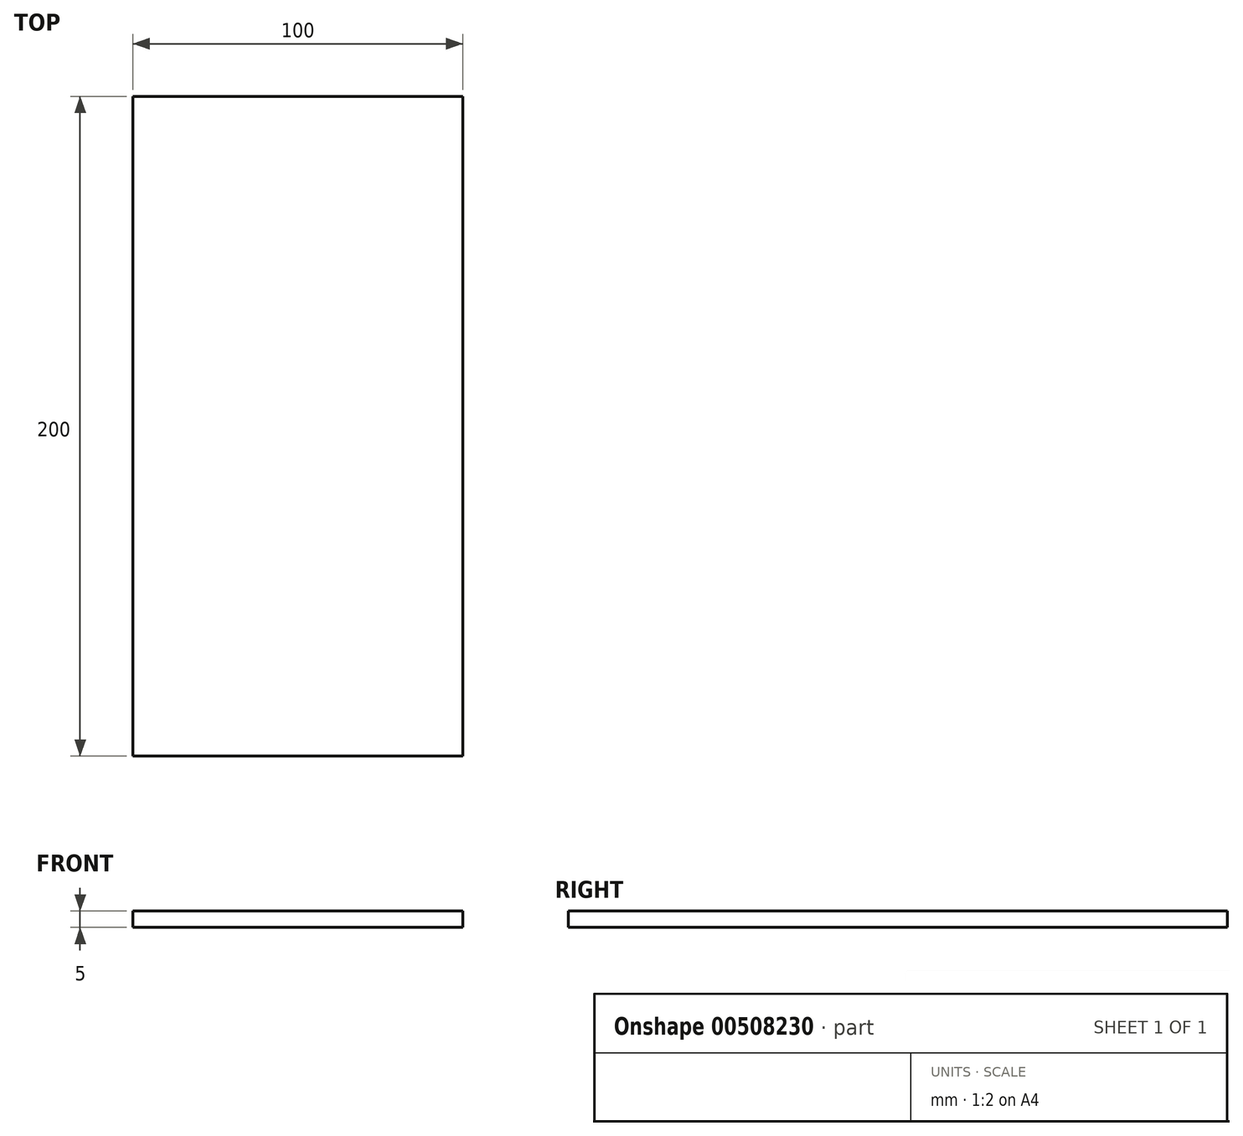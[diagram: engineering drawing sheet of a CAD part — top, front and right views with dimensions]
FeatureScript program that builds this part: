
annotation { "Feature Type Name" : "Feature", "Feature Type Description" : "" }
export const myFeature = defineFeature(function(context is Context, id is Id, definition is map)
    precondition{}
    {
        {
            var Q0;
            Q0=qCreatedBy(makeId("Top.planeOp"),FACE);
            var sketch = newSketch(context, id + "F0", { "sketchPlane" : qUnion([Q0])});
            skLineSegment(sketch, "E0.bottom", {"start": v(-50, 100) * mm, "end": v(50, 100) * mm});
            skLineSegment(sketch, "E0.top", {"start": v(-50, -100) * mm, "end": v(50, -100) * mm});
            skLineSegment(sketch, "E0.left", {"start": v(-50, 100) * mm, "end": v(-50, -100) * mm});
            skLineSegment(sketch, "E0.right", {"start": v(50, 100) * mm, "end": v(50, -100) * mm});
            skPoint(sketch, "E0.middle", {"position": v(0, 0) * mm});
            skSolve(sketch);
        }
        {
            var Q0;
            Q0=makeQuery(id+"F0.imprint","IMPRINT",FACE,{"disambiguationData":[TD([[makeQuery(id+"F0.imprint","IMPRINT",EDGE,{"derivedFrom":sQuery(id+"F0.wireOp",EDGE,"E0.bottom")}),-1.0]])]});
            extrude(context, id + "F1", {"entities" : qUnion([Q0]), "depth" : 5 * mm});
        }
    });
